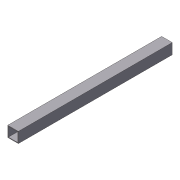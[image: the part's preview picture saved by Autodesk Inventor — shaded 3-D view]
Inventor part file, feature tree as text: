
AUTODESK INVENTOR PART (.ipt)
format: ipt  version: 2012 (Build 160160000, 160)  size: 71,680 bytes
history: native  units: in
note: dims shown in document units (in); Inventor stores cm internally (conversion verified against a paired STEP export)
features: extrude x1, shell x1, sketch x1
ambient origin geometry x8: Origin, YZ Plane, XZ Plane, XY Plane, X Axis, Y Axis, Z Axis, Center Point
bodies: Solid1 (feature_tree)
feature tree (3):
  extrude  "Extrusion1"  Depth=1.0in
  shell  "Shell1"  Thickness=14.5in
  sketch  "Sketch1"  dims[d0=1.0in d1=1.0in d2=14.5in d3=0.0in d4=0.0625in]
